# Revit family: BC_Aircalo_Fun40-IU-droite_LOD200_
name_source: partatom
category: Equipement de génie climatique
revit_build: Autodesk Revit 2017 (Build: 20160225_1515(x64)
units: mm (PartAtom-declared; Revit-internal decimal feet)

## family parameters
Basée sur le plan de construction = Non
Cote de connecteur circulaire = Utiliser le diamètre
Couper avec des vides une fois chargée = Non
Numéro OmniClass = 23.75.70.17.27
Partagée = Non
Point de calcul de pièce = Non
Titre OmniClass = Fan Coil Units
Toujours verticalement = Non
Type d'élément = Normal

## types (1)
- FUN 40 I/U Std - Servitude Droite
    Commentaires du type = FUN 40 I/U Std - Servitude Droite
    Connection Diameter = 13 mm
    Exhaust air diameter = 200 mm
    Fabricant = Aircalo
    Insulation Material = Polyurethane foam fireproof
    Main Material = Galvanized steel
    Mass = 22.00 kg
    Modèle = Ventilo-convecteur gainable FUN 40
    Motor power absorbed = 100 W
    New Air Radius = 63 mm
    Nominal Voltage = 230 V
    Outlet Diameter = 16 mm
    Overall Height = 237 mm
    Overall Length = 870 mm
    Overall Width = 716 mm
    Service Area Material = Service Area

## geometry (parser evidence)
native form markers: Sweep x3
no freeform markers — native parametric forms only
